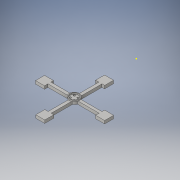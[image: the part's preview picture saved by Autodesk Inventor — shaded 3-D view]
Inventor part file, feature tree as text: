
AUTODESK INVENTOR PART (.ipt)
format: ipt  version: 2016 (Build 200138000, 138)  size: 167,424 bytes
history: native  units: in
note: dims shown in document units (in); Inventor stores cm internally (conversion verified against a paired STEP export)
features: hole x4, sketch x3, extrude x2
ambient origin geometry x8: Origin, YZ Plane, XZ Plane, XY Plane, X Axis, Y Axis, Z Axis, Center Point
bodies: Solid1 (feature_tree)
feature tree (9):
  extrude  "Extrusion1"  Depth=0.11in TaperAngle=0.0deg
  extrude  "Extrusion2"  Depth=0.15in
  sketch  "Sketch3"  dims[d32=0.15in d33=0.75in d34=0.19in d35=0.15in d36=0.5635in d37=1.0in d38=0.8108in d39=1.0in d40=1.0in d41=0.15in d42=0.75in d43=0.19in d44=0.15in d45=0.5635in d46=1.0in d47=0.8108in d48=1.0in d49=1.0in d50=0.15in d51=0.75in d52=0.19in d53=0.15in d54=0.5635in d55=1.0in d56=0.8108in d57=1.0in d58=1.0in d59=0.15in d60=0.75in d61=0.19in d62=0.15in d63=0.5635in d64=1.0in d65=0.8108in]
  hole  "Hole1"  [1 undecoded]
  hole  "Hole2"  [1 undecoded]
  hole  "Hole3"  [1 undecoded]
  hole  "Hole4"  [1 undecoded]
  sketch  "Sketch1"  dims[d26=0.25in d27=0.0in d28=0.11in d29=0.0in]
  sketch  "Sketch2"  dims[d30=1.0in d31=1.0in]
note: 4 required parameter values undecoded (feature->parameter linkage not recoverable at this tier; creation-order binding heuristic only, values carry confidence <= 0.55)
